# Revit family: VHS-UN_Angle_DN15-20_RFA
name_source: partatom
category: Pipe Accessories
units: mm (PartAtom-declared; Revit-internal decimal feet)

## family parameters
Always vertical = Yes
Cut with Voids When Loaded = No
OmniClass Number = 23.65.55.14.17
OmniClass Title = Adjusting/Controlling Valves for Liquid Services
Part Type = Valve - Breaks Into
Round Connector Dimension = Use Diameter
Shared = No
Work Plane-Based = No

## types (2) — shared parameters
Application = 2-pipe system
D = 20 mm  [stored 0.0656168 ft]
Description = Thermostatic H-piece Valve
H0 = 41 mm
H1 = 26 mm  [stored 0.0853018 ft]
H2 = 3 mm  [stored 0.00984252 ft]
H3 = 3.3 mm
H4 = 17 mm
H5 = 2.6 mm
H6 = 3.6 mm
HH = 46 mm  [stored 0.150919 ft]
IfcExportAs = IfcValveType
IfcExportType = VHS-UN
Kvs = 0.6 m³/h
L1 = 3 mm  [stored 0.00984252 ft]
L1__ve = -3 mm
L3 = 3.4 mm
L4 = 3.7 mm
L4_ve = -3.7 mm  [stored -0.0121391 ft]
L5_ve = -5 mm  [stored -0.0164042 ft]
L6_ve = -1.5 mm  [stored -0.00492126 ft]
L7_ve = -9.9 mm
LC1 = 50 mm
LL1 = 48.4 mm
LL2 = 22.2 mm  [stored 0.0728346 ft]
LL3 = 8.1 mm
LL4 = -0.4 mm
LL5 = 12 mm  [stored 0.0393701 ft]
LM = 25 mm  [stored 0.082021 ft]
LOD 200 = No
LOD 350 = Yes
L_EQ = 25 mm  [stored 0.082021 ft]
Manufacturer = Danfoss
Max Differential Pressure = 0.6 bar
Max Medium Temperature = 120 °C
Max Operating Pressure = 10 bar
RB1 = 11.7 mm  [stored 0.0383858 ft]
RB2 = 10.3 mm
RV1 = 10.5 mm  [stored 0.0344488 ft]
RV10 = 13.2 mm
RV2 = 12.5 mm  [stored 0.0410105 ft]
RV3 = 12.3 mm
RV4 = 11.4 mm
RV5 = 8 mm  [stored 0.0262467 ft]
RV6 = 10 mm  [stored 0.0328084 ft]
RV7 = 9.5 mm  [stored 0.031168 ft]
RV8 = 1 mm  [stored 0.00328084 ft]
RV9 = 15 mm  [stored 0.0492126 ft]
R_nut = 16.8 mm  [stored 0.0551181 ft]
TD1 = 33.5 mm  [stored 0.109908 ft]
TD2 = 26.4 mm
TH1 = 47.3 mm
URL = https://store.danfoss.com
Valve Body Material = Danfoss Nickel Plated Brass
W1 = 13.5 mm  [stored 0.0442913 ft]
W2 = 26 mm  [stored 0.0853018 ft]
W_nut1 = 14.5 mm
W_nut2 = 5.2 mm
zero-valued in all types: L2, L2_ve, LC2

## per-type parameters (varying)
| type | DR | Model | Model Type | Weight |
| VHS-UN_Angle_DN15-20_013G4741 | 15 mm | 013G4741 | VHS-UN_Angle_DN15-20 | 0.77 kg |
| VHS-UN_Angle_DN20-20_013G4743 | 20 mm | 013G4743 | VHS-UN_Angle_DN20-20 | 0.70 kg |

note: [stored X ft] marks values corroborated as IEEE doubles in the binary element streams (Revit-internal decimal feet)

## geometry (parser evidence)
native form markers: Sweep x4
no freeform markers — native parametric forms only
